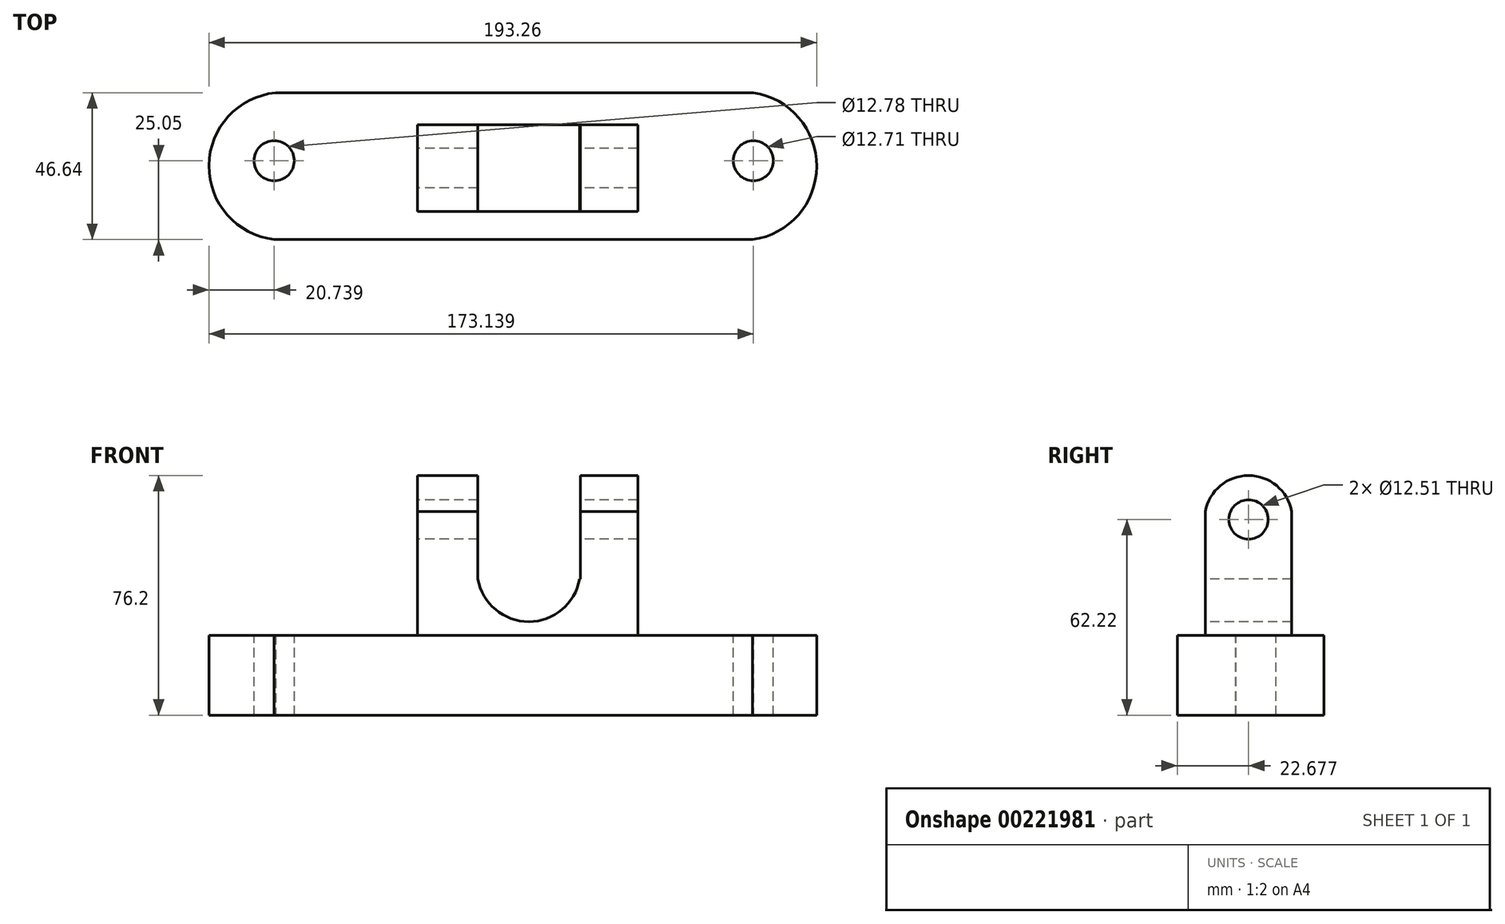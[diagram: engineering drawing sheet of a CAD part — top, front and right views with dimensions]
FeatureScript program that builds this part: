
annotation { "Feature Type Name" : "Feature", "Feature Type Description" : "" }
export const myFeature = defineFeature(function(context is Context, id is Id, definition is map)
    precondition{}
    {
        {
            var Q0;
            Q0=qCreatedBy(makeId("Top.planeOp"),FACE);
            var sketch = newSketch(context, id + "F0", { "sketchPlane" : qUnion([Q0])});
            skArc(sketch, "E0", {"start": v(-75.97, 21.6) * mm, "mid": v(-97.17, -1.52) * mm, "end": v(-76.43, -25.05) * mm});
            skLineSegment(sketch, "E1", {"start": v(-75.97, 21.6) * mm, "end": v(75.97, 21.6) * mm});
            skLineSegment(sketch, "E2", {"start": v(-76.43, -25.05) * mm, "end": v(75.74, -25.05) * mm});
            skArc(sketch, "E3", {"start": v(75.74, -25.05) * mm, "mid": v(96.1, -1.83) * mm, "end": v(75.97, 21.6) * mm});
            skSolve(sketch);
        }
        {
            var Q0;
            Q0 = qSketchRegion(id + "F0", true);
            extrude(context, id + "F1", {"entities" : qUnion([Q0]), "depth" : 25.4 * mm});
        }
        {
            var Q0;
            Q0=makeQuery(id+"F1.opExtrude","CAP_FACE",FACE,{"disambiguationData":[OSD([sQuery(id+"F0.wireOp",EDGE,"E0"),sQuery(id+"F0.wireOp",EDGE,"E1"),sQuery(id+"F0.wireOp",EDGE,"E2"),sQuery(id+"F0.wireOp",EDGE,"E3")])],"isStart":false});
            var sketch = newSketch(context, id + "F2", { "sketchPlane" : qUnion([Q0])});
            skCircle(sketch, "E4", {"center": v(-76.43, 0) * mm, "radius": 6.4 * mm});
            skSolve(sketch);
        }
        {
            var Q0;
            Q0 = qSketchRegion(id + "F2", true);
            extrude(context, id + "F3", {"entities" : qUnion([Q0]), "operationType" : NewBodyOperationType.REMOVE, "endBound" : BoundingType.THROUGH_ALL, "oppositeDirection" : true, "depth" : 25.4 * mm});
        }
        {
            var Q0;
            Q0=makeQuery(id+"F1.opExtrude","CAP_FACE",FACE,{"disambiguationData":[OSD([sQuery(id+"F0.wireOp",EDGE,"E0"),sQuery(id+"F0.wireOp",EDGE,"E1"),sQuery(id+"F0.wireOp",EDGE,"E2"),sQuery(id+"F0.wireOp",EDGE,"E3")])],"isStart":false});
            var sketch = newSketch(context, id + "F4", { "sketchPlane" : qUnion([Q0])});
            skCircle(sketch, "E5", {"center": v(75.97, 0) * mm, "radius": 6.35 * mm});
            skSolve(sketch);
        }
        {
            var Q0;
            Q0 = qSketchRegion(id + "F4", true);
            extrude(context, id + "F5", {"entities" : qUnion([Q0]), "operationType" : NewBodyOperationType.REMOVE, "endBound" : BoundingType.THROUGH_ALL, "oppositeDirection" : true, "depth" : 25.4 * mm});
        }
        {
            var Q0;
            Q0=makeQuery(id+"F1.opExtrude","CAP_FACE",FACE,{"disambiguationData":[OSD([sQuery(id+"F0.wireOp",EDGE,"E0"),sQuery(id+"F0.wireOp",EDGE,"E1"),sQuery(id+"F0.wireOp",EDGE,"E2"),sQuery(id+"F0.wireOp",EDGE,"E3")])],"isStart":false});
            var sketch = newSketch(context, id + "F6", { "sketchPlane" : qUnion([Q0])});
            skLineSegment(sketch, "E6.bottom", {"start": v(-30.83, 11.37) * mm, "end": v(39.2, 11.37) * mm});
            skLineSegment(sketch, "E6.top", {"start": v(-30.83, -16.12) * mm, "end": v(39.2, -16.12) * mm});
            skLineSegment(sketch, "E6.left", {"start": v(-30.83, 11.37) * mm, "end": v(-30.83, -16.12) * mm});
            skLineSegment(sketch, "E6.right", {"start": v(39.2, 11.37) * mm, "end": v(39.2, -16.12) * mm});
            skSolve(sketch);
        }
        {
            var Q0;
            Q0 = qSketchRegion(id + "F6", true);
            extrude(context, id + "F7", {"entities" : qUnion([Q0]), "operationType" : NewBodyOperationType.ADD, "depth" : 50.8 * mm});
        }
        {
            var Q0;
            Q0=makeQuery(id+"F7.opExtrude","SWEPT_FACE",FACE,{"disambiguationData":[OSD([sQuery(id+"F6.wireOp",EDGE,"E6.left")])]});
            var sketch = newSketch(context, id + "F8", { "sketchPlane" : qUnion([Q0])});
            skLineSegment(sketch, "E7", {"start": v(2.37, 76.2) * mm, "end": v(-11.37, 76.2) * mm});
            skLineSegment(sketch, "E8", {"start": v(-11.37, 76.2) * mm, "end": v(-11.37, 64.77) * mm});
            skArc(sketch, "E9", {"start": v(2.37, 76.2) * mm, "mid": v(-6.57, 72.97) * mm, "end": v(-11.37, 64.77) * mm});
            skLineSegment(sketch, "E10", {"start": v(2.37, 76.2) * mm, "end": v(16.12, 76.2) * mm});
            skLineSegment(sketch, "E11", {"start": v(16.12, 76.2) * mm, "end": v(16.12, 64.77) * mm});
            skArc(sketch, "E12", {"start": v(16.12, 64.77) * mm, "mid": v(11.31, 72.97) * mm, "end": v(2.37, 76.2) * mm});
            skSolve(sketch);
        }
        {
            var Q0;
            Q0 = qSketchRegion(id + "F8", true);
            extrude(context, id + "F9", {"entities" : qUnion([Q0]), "operationType" : NewBodyOperationType.REMOVE, "endBound" : BoundingType.THROUGH_ALL, "oppositeDirection" : true, "depth" : 25.4 * mm});
        }
        {
            var Q0;
            Q0=makeQuery(id+"F7.opExtrude","SWEPT_FACE",FACE,{"disambiguationData":[OSD([sQuery(id+"F6.wireOp",EDGE,"E6.left")])]});
            var sketch = newSketch(context, id + "F10", { "sketchPlane" : qUnion([Q0])});
            skCircle(sketch, "E13", {"center": v(2.37, 62.22) * mm, "radius": 6.26 * mm});
            skSolve(sketch);
        }
        {
            var Q0;
            Q0 = qSketchRegion(id + "F10", true);
            extrude(context, id + "F11", {"entities" : qUnion([Q0]), "operationType" : NewBodyOperationType.REMOVE, "endBound" : BoundingType.THROUGH_ALL, "oppositeDirection" : true, "depth" : 25.4 * mm});
        }
        {
            var Q0;
            Q0=makeQuery(id+"F7.opExtrude","SWEPT_FACE",FACE,{"disambiguationData":[OSD([sQuery(id+"F6.wireOp",EDGE,"E6.top")])]});
            var sketch = newSketch(context, id + "F12", { "sketchPlane" : qUnion([Q0])});
            skLineSegment(sketch, "E14.top", {"start": v(-11.63, 43.3) * mm, "end": v(20.7, 43.3) * mm});
            skArc(sketch, "E15", {"start": v(-11.63, 43.3) * mm, "mid": v(4.53, 29.73) * mm, "end": v(20.7, 43.3) * mm});
            skLineSegment(sketch, "E16.bottom", {"start": v(-11.63, 43.3) * mm, "end": v(20.93, 43.3) * mm});
            skLineSegment(sketch, "E16.top", {"start": v(-11.63, 78.86) * mm, "end": v(20.93, 78.86) * mm});
            skLineSegment(sketch, "E16.left", {"start": v(-11.63, 43.3) * mm, "end": v(-11.63, 78.86) * mm});
            skLineSegment(sketch, "E16.right", {"start": v(20.93, 43.3) * mm, "end": v(20.93, 78.86) * mm});
            skSolve(sketch);
        }
        {
            var Q0;
            Q0 = qSketchRegion(id + "F12", true);
            extrude(context, id + "F13", {"entities" : qUnion([Q0]), "operationType" : NewBodyOperationType.REMOVE, "endBound" : BoundingType.THROUGH_ALL, "oppositeDirection" : true, "depth" : 25.4 * mm});
        }
    });
